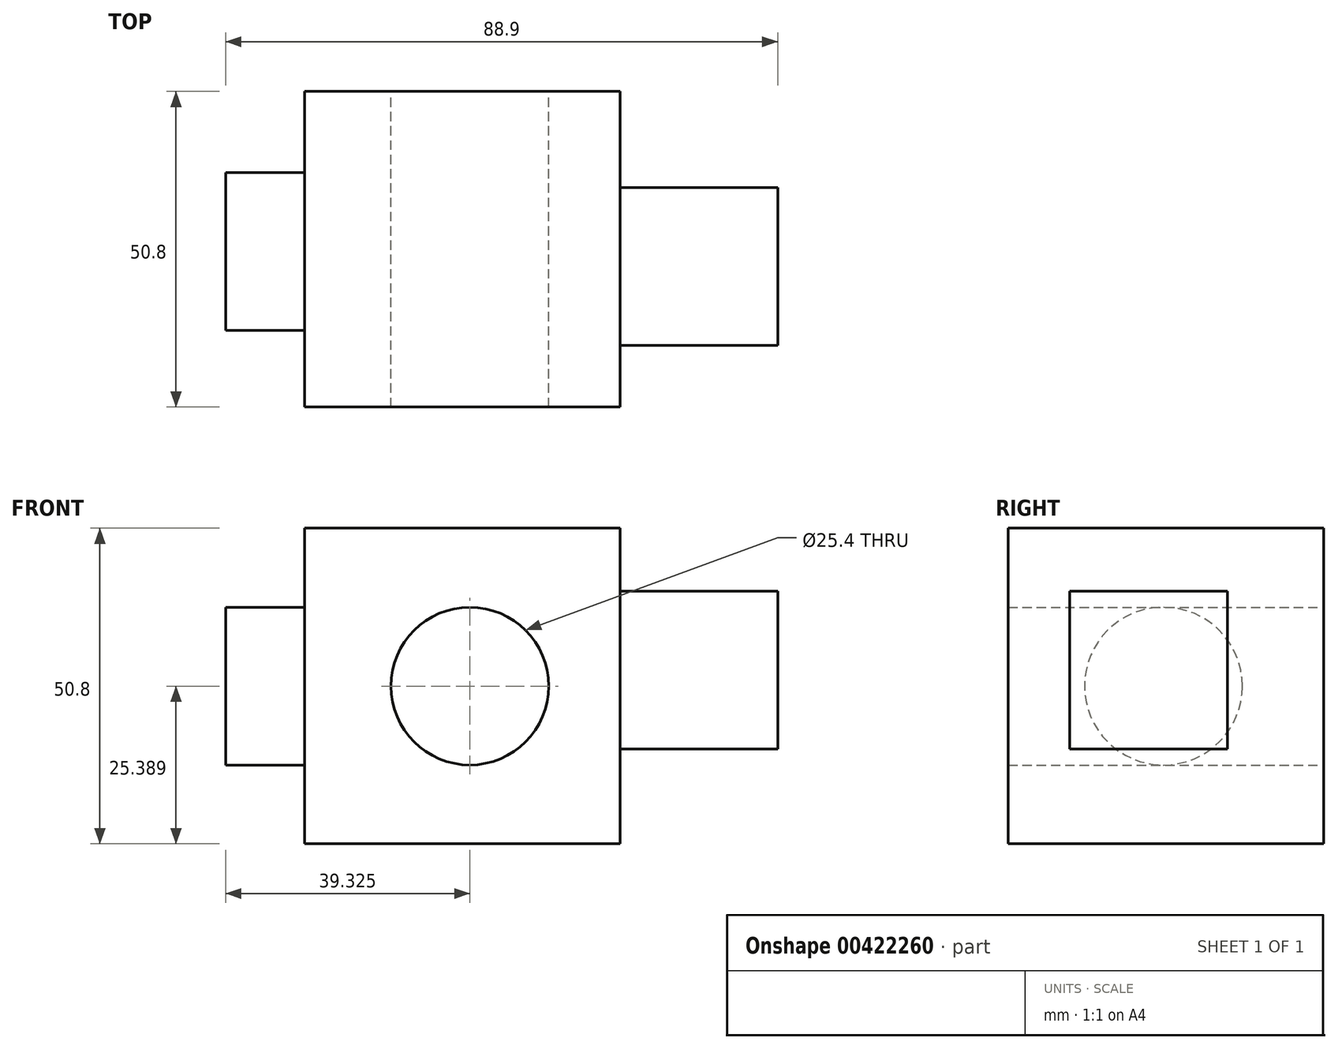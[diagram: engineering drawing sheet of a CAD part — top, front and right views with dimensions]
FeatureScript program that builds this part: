
annotation { "Feature Type Name" : "Feature", "Feature Type Description" : "" }
export const myFeature = defineFeature(function(context is Context, id is Id, definition is map)
    precondition{}
    {
        {
            var Q0;
            Q0=qCreatedBy(makeId("Front.planeOp"),FACE);
            var sketch = newSketch(context, id + "F0", { "sketchPlane" : qUnion([Q0])});
            skLineSegment(sketch, "E0.bottom", {"start": v(0, 0) * mm, "end": v(-50.8, 0) * mm});
            skLineSegment(sketch, "E0.top", {"start": v(0, 50.8) * mm, "end": v(-50.8, 50.8) * mm});
            skLineSegment(sketch, "E0.left", {"start": v(0, 0) * mm, "end": v(0, 50.8) * mm});
            skLineSegment(sketch, "E0.right", {"start": v(-50.8, 0) * mm, "end": v(-50.8, 50.8) * mm});
            skSolve(sketch);
        }
        {
            var Q0;
            Q0=qCreatedBy(makeId("Front.planeOp"),FACE);
            var sketch = newSketch(context, id + "F1", { "sketchPlane" : qUnion([Q0])});
            skCircle(sketch, "E1", {"center": v(-24.17, 25.39) * mm, "radius": 12.7 * mm});
            skSolve(sketch);
        }
        {
            var Q0;
            Q0=makeQuery(id+"F0.imprint","IMPRINT",FACE,{"disambiguationData":[TD([[makeQuery(id+"F0.imprint","IMPRINT",EDGE,{"derivedFrom":sQuery(id+"F0.wireOp",EDGE,"E0.bottom")}),-1.0]])]});
            extrude(context, id + "F2", {"entities" : qUnion([Q0]), "depth" : 50.8 * mm});
        }
        {
            var Q0;
            Q0=makeQuery(id+"F1.imprint","IMPRINT",FACE,{"disambiguationData":[TD([[makeQuery(id+"F1.imprint","IMPRINT",EDGE,{"derivedFrom":sQuery(id+"F1.wireOp",EDGE,"E1")}),1.0]])]});
            extrude(context, id + "F3", {"entities" : qUnion([Q0]), "operationType" : NewBodyOperationType.REMOVE, "oppositeDirection" : true, "depth" : -50.8 * mm});
        }
        {
            var Q0;
            Q0=makeQuery(id+"F2.opExtrude","SWEPT_FACE",FACE,{"disambiguationData":[OSD([sQuery(id+"F0.wireOp",EDGE,"E0.right")])]});
            var sketch = newSketch(context, id + "F4", { "sketchPlane" : qUnion([Q0])});
            skCircle(sketch, "E2", {"center": v(25.8, 25.39) * mm, "radius": 12.7 * mm});
            skSolve(sketch);
        }
        {
            var Q0;
            Q0=makeQuery(id+"F4.imprint","IMPRINT",FACE,{"disambiguationData":[TD([[makeQuery(id+"F4.imprint","IMPRINT",EDGE,{"derivedFrom":sQuery(id+"F4.wireOp",EDGE,"E2")}),1.0]])]});
            extrude(context, id + "F5", {"entities" : qUnion([Q0]), "operationType" : NewBodyOperationType.ADD, "depth" : 12.7 * mm});
        }
        {
            var Q0;
            Q0=qCreatedBy(makeId("Right.planeOp"),FACE);
            var sketch = newSketch(context, id + "F6", { "sketchPlane" : qUnion([Q0])});
            skLineSegment(sketch, "E3.bottom", {"start": v(-40.88, 40.67) * mm, "end": v(-15.48, 40.67) * mm});
            skLineSegment(sketch, "E3.top", {"start": v(-40.88, 15.27) * mm, "end": v(-15.48, 15.27) * mm});
            skLineSegment(sketch, "E3.left", {"start": v(-40.88, 40.67) * mm, "end": v(-40.88, 15.27) * mm});
            skLineSegment(sketch, "E3.right", {"start": v(-15.48, 40.67) * mm, "end": v(-15.48, 15.27) * mm});
            skSolve(sketch);
        }
        {
            var Q0;
            Q0=makeQuery(id+"F6.imprint","IMPRINT",FACE,{"disambiguationData":[TD([[makeQuery(id+"F6.imprint","IMPRINT",EDGE,{"derivedFrom":sQuery(id+"F6.wireOp",EDGE,"E3.bottom")}),-1.0]])]});
            extrude(context, id + "F7", {"entities" : qUnion([Q0]), "operationType" : NewBodyOperationType.ADD, "depth" : 25.4 * mm});
        }
    });
